# Revit family: DQ
name_source: partatom
category: Wyposażenie mechaniczne
revit_build: Autodesk Revit 2017 (Build: 20160225_1515(x64)
units: mm (PartAtom-declared; Revit-internal decimal feet)

## family parameters
Oparty na płaszczyźnie roboczej = Nie
Punkt obliczania pomieszczeń = Nie
Tnij formami wycięć po wczytaniu = Nie
Typ części = Normalny
Współdzielony = Nie
Wymiar okrągłego złącza = Użyj średnicy
Zawsze pionowo = Tak

## types (30) — shared parameters
Date = 01.2019
Frequency = 50 Hz
Producent = Rosenberg
URL = https://www.rosenberg.pl
Version = 1

## per-type parameters (varying)
- 400-4.4EC: 250_cover=Nie; 300_cover=Nie; 350_cover=Nie; 400_cover=Tak; 450_cover=Nie; 500_cover=Nie; 560_cover=Nie; 630_cover=Nie; 710_cover=Nie; 800_cover=Nie; Air_flow=3121.0 m³/h; Current=0 A; Electrical_motor_diameter=30 mm  [stored 0.0984252 ft]; Electrical_motor_length_back=60 mm  [stored 0.19685 ft]; Electrical_motor_length_front=50 mm  [stored 0.164042 ft]; Housing_dimension=540 mm; Housing_dimension/2=270 mm; Inner_diameter=403 mm; Outer_diameter=437 mm; Power=0 kW; Pressure=66.0 Pa; Propeller_length=197 mm  [stored 0.646325 ft]; Protection_class=IP54; Radius_inner=202 mm; Radius_outer=219 mm; Sheet_metal_thickness=12 mm  [stored 0.0393701 ft]; Thickness=88 mm  [stored 0.288714 ft]; Voltage=400 V; Weight=8.00 kg; max.Ambient_temperature=65 °C
- 250-2.3DF: 250_cover=Tak; 300_cover=Nie; 350_cover=Nie; 400_cover=Nie; 450_cover=Nie; 500_cover=Nie; 560_cover=Nie; 630_cover=Nie; 710_cover=Nie; 800_cover=Nie; Air_flow=0.0 m³/h; Current=0 A; Electrical_motor_diameter=30 mm  [stored 0.0984252 ft]; Electrical_motor_length_back=85 mm  [stored 0.278871 ft]; Electrical_motor_length_front=8 mm  [stored 0.0262467 ft]; Housing_dimension=370 mm; Housing_dimension/2=185 mm  [stored 0.606955 ft]; Inner_diameter=254 mm; Outer_diameter=275 mm; Power=0 kW; Pressure=0.0 Pa; Propeller_length=122 mm; Protection_class=IP44; Radius_inner=127 mm; Radius_outer=138 mm; Sheet_metal_thickness=6 mm  [stored 0.019685 ft]; Thickness=49 mm  [stored 0.160761 ft]; Voltage=400 V; Weight=4.30 kg; max.Ambient_temperature=70 °C
- 350-2: 250_cover=Nie; 300_cover=Nie; 350_cover=Tak; 400_cover=Nie; 450_cover=Nie; 500_cover=Nie; 560_cover=Nie; 630_cover=Nie; 710_cover=Nie; 800_cover=Nie; Air_flow=3693.0 m³/h; Current=2 A; Electrical_motor_diameter=30 mm  [stored 0.0984252 ft]; Electrical_motor_length_back=60 mm  [stored 0.19685 ft]; Electrical_motor_length_front=41 mm  [stored 0.134514 ft]; Housing_dimension=485 mm; Housing_dimension/2=243 mm; Inner_diameter=358 mm; Outer_diameter=381 mm; Power=1 kW; Pressure=223.0 Pa; Propeller_length=174 mm  [stored 0.570866 ft]; Protection_class=IP54; Radius_inner=179 mm  [stored 0.58727 ft]; Radius_outer=191 mm; Sheet_metal_thickness=12 mm  [stored 0.0393701 ft]; Thickness=74 mm  [stored 0.242782 ft]; Voltage=400 V; Weight=13.00 kg; max.Ambient_temperature=55 °C
- 250-4.3CF: 250_cover=Tak; 300_cover=Nie; 350_cover=Nie; 400_cover=Nie; 450_cover=Nie; 500_cover=Nie; 560_cover=Nie; 630_cover=Nie; 710_cover=Nie; 800_cover=Nie; Air_flow=0.0 m³/h; Current=0 A; Electrical_motor_diameter=30 mm  [stored 0.0984252 ft]; Electrical_motor_length_back=85 mm  [stored 0.278871 ft]; Electrical_motor_length_front=8 mm  [stored 0.0262467 ft]; Housing_dimension=370 mm; Housing_dimension/2=185 mm  [stored 0.606955 ft]; Inner_diameter=254 mm; Outer_diameter=275 mm; Power=0 kW; Pressure=0.0 Pa; Propeller_length=122 mm; Protection_class=IP44; Radius_inner=127 mm; Radius_outer=138 mm; Sheet_metal_thickness=6 mm  [stored 0.019685 ft]; Thickness=78 mm  [stored 0.255906 ft]; Voltage=230 V; Weight=4.00 kg; max.Ambient_temperature=70 °C
- 315-2: 250_cover=Nie; 300_cover=Tak; 350_cover=Nie; 400_cover=Nie; 450_cover=Nie; 500_cover=Nie; 560_cover=Nie; 630_cover=Nie; 710_cover=Nie; 800_cover=Nie; Air_flow=2675.0 m³/h; Current=1 A; Electrical_motor_diameter=30 mm  [stored 0.0984252 ft]; Electrical_motor_length_back=60 mm  [stored 0.19685 ft]; Electrical_motor_length_front=5 mm  [stored 0.0164042 ft]; Housing_dimension=430 mm; Housing_dimension/2=215 mm; Inner_diameter=317 mm; Outer_diameter=330 mm; Power=1 kW; Pressure=188.0 Pa; Propeller_length=154 mm; Protection_class=IP54; Radius_inner=159 mm; Radius_outer=165 mm; Sheet_metal_thickness=11 mm  [stored 0.0360892 ft]; Thickness=71 mm  [stored 0.23294 ft]; Voltage=400 V; Weight=9.00 kg; max.Ambient_temperature=60 °C
- 315-2.4FF: 250_cover=Nie; 300_cover=Tak; 350_cover=Nie; 400_cover=Nie; 450_cover=Nie; 500_cover=Nie; 560_cover=Nie; 630_cover=Nie; 710_cover=Nie; 800_cover=Nie; Air_flow=2310.0 m³/h; Current=1 A; Electrical_motor_diameter=30 mm  [stored 0.0984252 ft]; Electrical_motor_length_back=60 mm  [stored 0.19685 ft]; Electrical_motor_length_front=5 mm  [stored 0.0164042 ft]; Housing_dimension=430 mm; Housing_dimension/2=215 mm; Inner_diameter=317 mm; Outer_diameter=330 mm; Power=0 kW; Pressure=216.0 Pa; Propeller_length=154 mm; Protection_class=IP54; Radius_inner=159 mm; Radius_outer=165 mm; Sheet_metal_thickness=11 mm  [stored 0.0360892 ft]; Thickness=71 mm  [stored 0.23294 ft]; Voltage=40 V; Weight=5.50 kg; max.Ambient_temperature=50 °C
- 315-4.4DA: 250_cover=Nie; 300_cover=Tak; 350_cover=Nie; 400_cover=Nie; 450_cover=Nie; 500_cover=Nie; 560_cover=Nie; 630_cover=Nie; 710_cover=Nie; 800_cover=Nie; Air_flow=0.0 m³/h; Current=0 A; Electrical_motor_diameter=30 mm  [stored 0.0984252 ft]; Electrical_motor_length_back=60 mm  [stored 0.19685 ft]; Electrical_motor_length_front=5 mm  [stored 0.0164042 ft]; Housing_dimension=430 mm; Housing_dimension/2=215 mm; Inner_diameter=317 mm; Outer_diameter=330 mm; Power=0 kW; Pressure=0.0 Pa; Propeller_length=154 mm; Protection_class=IP54; Radius_inner=159 mm; Radius_outer=165 mm; Sheet_metal_thickness=11 mm  [stored 0.0360892 ft]; Thickness=71 mm  [stored 0.23294 ft]; Voltage=400 V; Weight=5.50 kg; max.Ambient_temperature=60 °C
- 350-4: 250_cover=Nie; 300_cover=Nie; 350_cover=Tak; 400_cover=Nie; 450_cover=Nie; 500_cover=Nie; 560_cover=Nie; 630_cover=Nie; 710_cover=Nie; 800_cover=Nie; Air_flow=2213.0 m³/h; Current=0 A; Electrical_motor_diameter=30 mm  [stored 0.0984252 ft]; Electrical_motor_length_back=60 mm  [stored 0.19685 ft]; Electrical_motor_length_front=41 mm  [stored 0.134514 ft]; Housing_dimension=485 mm; Housing_dimension/2=243 mm; Inner_diameter=358 mm; Outer_diameter=381 mm; Power=0 kW; Pressure=59.0 Pa; Propeller_length=174 mm  [stored 0.570866 ft]; Protection_class=IP54; Radius_inner=179 mm  [stored 0.58727 ft]; Radius_outer=191 mm; Sheet_metal_thickness=12 mm  [stored 0.0393701 ft]; Thickness=74 mm  [stored 0.242782 ft]; Voltage=400 V; Weight=6.50 kg; max.Ambient_temperature=65 °C
- 350-4.4EC: 250_cover=Nie; 300_cover=Nie; 350_cover=Tak; 400_cover=Nie; 450_cover=Nie; 500_cover=Nie; 560_cover=Nie; 630_cover=Nie; 710_cover=Nie; 800_cover=Nie; Air_flow=2079.0 m³/h; Current=0 A; Electrical_motor_diameter=30 mm  [stored 0.0984252 ft]; Electrical_motor_length_back=60 mm  [stored 0.19685 ft]; Electrical_motor_length_front=41 mm  [stored 0.134514 ft]; Housing_dimension=485 mm; Housing_dimension/2=243 mm; Inner_diameter=358 mm; Outer_diameter=381 mm; Power=0 kW; Pressure=82.0 Pa; Propeller_length=174 mm  [stored 0.570866 ft]; Protection_class=IP54; Radius_inner=179 mm  [stored 0.58727 ft]; Radius_outer=191 mm; Sheet_metal_thickness=12 mm  [stored 0.0393701 ft]; Thickness=74 mm  [stored 0.242782 ft]; Voltage=400 V; Weight=7.00 kg; max.Ambient_temperature=70 °C
- 400-6: 250_cover=Nie; 300_cover=Nie; 350_cover=Nie; 400_cover=Tak; 450_cover=Nie; 500_cover=Nie; 560_cover=Nie; 630_cover=Nie; 710_cover=Nie; 800_cover=Nie; Air_flow=2565.0 m³/h; Current=0 A; Electrical_motor_diameter=65 mm  [stored 0.213255 ft]; Electrical_motor_length_back=60 mm  [stored 0.19685 ft]; Electrical_motor_length_front=50 mm  [stored 0.164042 ft]; Housing_dimension=540 mm; Housing_dimension/2=270 mm; Inner_diameter=403 mm; Outer_diameter=437 mm; Power=0 kW; Pressure=46.0 Pa; Propeller_length=197 mm  [stored 0.646325 ft]; Protection_class=IP54; Radius_inner=202 mm; Radius_outer=219 mm; Sheet_metal_thickness=12 mm  [stored 0.0393701 ft]; Thickness=88 mm  [stored 0.288714 ft]; Voltage=400 V; Weight=9.00 kg; max.Ambient_temperature=60 °C
- 450-4.5DF: 250_cover=Nie; 300_cover=Nie; 350_cover=Nie; 400_cover=Nie; 450_cover=Tak; 500_cover=Nie; 560_cover=Nie; 630_cover=Nie; 710_cover=Nie; 800_cover=Nie; Air_flow=4246.0 m³/h; Current=1 A; Electrical_motor_diameter=65 mm  [stored 0.213255 ft]; Electrical_motor_length_back=60 mm  [stored 0.19685 ft]; Electrical_motor_length_front=50 mm  [stored 0.164042 ft]; Housing_dimension=575 mm; Housing_dimension/2=288 mm; Inner_diameter=452 mm; Outer_diameter=513 mm; Power=0 kW; Pressure=96.0 Pa; Propeller_length=221 mm; Protection_class=IP54; Radius_inner=226 mm; Radius_outer=257 mm; Sheet_metal_thickness=14 mm  [stored 0.0459318 ft]; Thickness=86 mm  [stored 0.282152 ft]; Voltage=400 V; Weight=10.50 kg; max.Ambient_temperature=60 °C
- 450-6.5DF: 250_cover=Nie; 300_cover=Nie; 350_cover=Nie; 400_cover=Nie; 450_cover=Tak; 500_cover=Nie; 560_cover=Nie; 630_cover=Nie; 710_cover=Nie; 800_cover=Nie; Air_flow=0.0 m³/h; Current=0 A; Electrical_motor_diameter=65 mm  [stored 0.213255 ft]; Electrical_motor_length_back=60 mm  [stored 0.19685 ft]; Electrical_motor_length_front=50 mm  [stored 0.164042 ft]; Housing_dimension=575 mm; Housing_dimension/2=288 mm; Inner_diameter=452 mm; Outer_diameter=513 mm; Power=0 kW; Pressure=0.0 Pa; Propeller_length=221 mm; Protection_class=IP54; Radius_inner=226 mm; Radius_outer=257 mm; Sheet_metal_thickness=14 mm  [stored 0.0459318 ft]; Thickness=86 mm  [stored 0.282152 ft]; Voltage=400 V; Weight=10.00 kg; max.Ambient_temperature=70 °C
- 500-4.5FA: 250_cover=Nie; 300_cover=Nie; 350_cover=Nie; 400_cover=Nie; 450_cover=Nie; 500_cover=Tak; 560_cover=Nie; 630_cover=Nie; 710_cover=Nie; 800_cover=Nie; Air_flow=5256.0 m³/h; Current=1 A; Electrical_motor_diameter=65 mm  [stored 0.213255 ft]; Electrical_motor_length_back=60 mm  [stored 0.19685 ft]; Electrical_motor_length_front=50 mm  [stored 0.164042 ft]; Housing_dimension=655 mm; Housing_dimension/2=328 mm; Inner_diameter=504 mm; Outer_diameter=540 mm; Power=0 kW; Pressure=105.0 Pa; Propeller_length=247 mm; Protection_class=IP54; Radius_inner=252 mm; Radius_outer=270 mm; Sheet_metal_thickness=16 mm  [stored 0.0524934 ft]; Thickness=104 mm  [stored 0.341207 ft]; Voltage=400 V; Weight=15.50 kg; max.Ambient_temperature=60 °C
- 560-4.5HA: 250_cover=Nie; 300_cover=Nie; 350_cover=Nie; 400_cover=Nie; 450_cover=Nie; 500_cover=Nie; 560_cover=Tak; 630_cover=Nie; 710_cover=Nie; 800_cover=Nie; Air_flow=6766.0 m³/h; Current=2 A; Electrical_motor_diameter=65 mm  [stored 0.213255 ft]; Electrical_motor_length_back=60 mm  [stored 0.19685 ft]; Electrical_motor_length_front=50 mm  [stored 0.164042 ft]; Housing_dimension=725 mm; Housing_dimension/2=363 mm; Inner_diameter=560 mm; Outer_diameter=597 mm; Power=1 kW; Pressure=136.0 Pa; Propeller_length=275 mm; Protection_class=IP54; Radius_inner=280 mm; Radius_outer=299 mm; Sheet_metal_thickness=16 mm  [stored 0.0524934 ft]; Thickness=104 mm  [stored 0.341207 ft]; Voltage=400 V; Weight=19.50 kg; max.Ambient_temperature=50 °C
- 560-6.5FA: 250_cover=Nie; 300_cover=Nie; 350_cover=Nie; 400_cover=Nie; 450_cover=Nie; 500_cover=Nie; 560_cover=Tak; 630_cover=Nie; 710_cover=Nie; 800_cover=Nie; Air_flow=5438.0 m³/h; Current=1 A; Electrical_motor_diameter=65 mm  [stored 0.213255 ft]; Electrical_motor_length_back=60 mm  [stored 0.19685 ft]; Electrical_motor_length_front=50 mm  [stored 0.164042 ft]; Housing_dimension=725 mm; Housing_dimension/2=363 mm; Inner_diameter=560 mm; Outer_diameter=597 mm; Power=0 kW; Pressure=69.0 Pa; Propeller_length=275 mm; Protection_class=IP54; Radius_inner=280 mm; Radius_outer=299 mm; Sheet_metal_thickness=16 mm  [stored 0.0524934 ft]; Thickness=104 mm  [stored 0.341207 ft]; Voltage=400 V; Weight=20.00 kg; max.Ambient_temperature=55 °C
- 630-4: 250_cover=Nie; 300_cover=Nie; 350_cover=Nie; 400_cover=Nie; 450_cover=Nie; 500_cover=Nie; 560_cover=Nie; 630_cover=Tak; 710_cover=Nie; 800_cover=Nie; Air_flow=12190.0 m³/h; Current=4 A; Electrical_motor_diameter=65 mm  [stored 0.213255 ft]; Electrical_motor_length_back=60 mm  [stored 0.19685 ft]; Electrical_motor_length_front=50 mm  [stored 0.164042 ft]; Housing_dimension=805 mm; Housing_dimension/2=403 mm; Inner_diameter=635 mm; Outer_diameter=683 mm; Power=2 kW; Pressure=209.0 Pa; Propeller_length=313 mm; Protection_class=IP44; Radius_inner=318 mm; Radius_outer=342 mm; Sheet_metal_thickness=20 mm  [stored 0.0656168 ft]; Thickness=130 mm  [stored 0.426509 ft]; Voltage=400 V; Weight=35.00 kg; max.Ambient_temperature=50 °C
- 630-6.5HA: 250_cover=Nie; 300_cover=Nie; 350_cover=Nie; 400_cover=Nie; 450_cover=Nie; 500_cover=Nie; 560_cover=Nie; 630_cover=Tak; 710_cover=Nie; 800_cover=Nie; Air_flow=7885.0 m³/h; Current=1 A; Electrical_motor_diameter=65 mm  [stored 0.213255 ft]; Electrical_motor_length_back=60 mm  [stored 0.19685 ft]; Electrical_motor_length_front=50 mm  [stored 0.164042 ft]; Housing_dimension=805 mm; Housing_dimension/2=403 mm; Inner_diameter=635 mm; Outer_diameter=683 mm; Power=1 kW; Pressure=74.0 Pa; Propeller_length=313 mm; Protection_class=IP54; Radius_inner=318 mm; Radius_outer=342 mm; Sheet_metal_thickness=20 mm  [stored 0.0656168 ft]; Thickness=130 mm  [stored 0.426509 ft]; Voltage=400 V; Weight=22.00 kg; max.Ambient_temperature=55 °C
- 710-6.6HF: 250_cover=Nie; 300_cover=Nie; 350_cover=Nie; 400_cover=Nie; 450_cover=Nie; 500_cover=Nie; 560_cover=Nie; 630_cover=Nie; 710_cover=Tak; 800_cover=Nie; Air_flow=10492.0 m³/h; Current=2 A; Electrical_motor_diameter=50 mm  [stored 0.164042 ft]; Electrical_motor_length_back=60 mm  [stored 0.19685 ft]; Electrical_motor_length_front=50 mm  [stored 0.164042 ft]; Housing_dimension=850 mm; Housing_dimension/2=425 mm; Inner_diameter=711 mm; Outer_diameter=772 mm; Power=1 kW; Pressure=104.0 Pa; Propeller_length=351 mm; Protection_class=IP54; Radius_inner=356 mm; Radius_outer=386 mm; Sheet_metal_thickness=20 mm  [stored 0.0656168 ft]; Thickness=150 mm; Voltage=400 V; Weight=36.00 kg; max.Ambient_temperature=70 °C
- 500-6.5DF: 250_cover=Nie; 300_cover=Nie; 350_cover=Nie; 400_cover=Nie; 450_cover=Nie; 500_cover=Tak; 560_cover=Nie; 630_cover=Nie; 710_cover=Nie; 800_cover=Nie; Air_flow=3433.0 m³/h; Current=0 A; Electrical_motor_diameter=65 mm  [stored 0.213255 ft]; Electrical_motor_length_back=60 mm  [stored 0.19685 ft]; Electrical_motor_length_front=50 mm  [stored 0.164042 ft]; Housing_dimension=655 mm; Housing_dimension/2=328 mm; Inner_diameter=504 mm; Outer_diameter=540 mm; Power=0 kW; Pressure=49.0 Pa; Propeller_length=247 mm; Protection_class=IP54; Radius_inner=252 mm; Radius_outer=270 mm; Sheet_metal_thickness=16 mm  [stored 0.0524934 ft]; Thickness=104 mm  [stored 0.341207 ft]; Voltage=400 V; Weight=16.00 kg; max.Ambient_temperature=70 °C
- 630-4.6LA: 250_cover=Nie; 300_cover=Nie; 350_cover=Nie; 400_cover=Nie; 450_cover=Nie; 500_cover=Nie; 560_cover=Nie; 630_cover=Tak; 710_cover=Nie; 800_cover=Nie; Air_flow=12440.0 m³/h; Current=4 A; Electrical_motor_diameter=65 mm  [stored 0.213255 ft]; Electrical_motor_length_back=60 mm  [stored 0.19685 ft]; Electrical_motor_length_front=50 mm  [stored 0.164042 ft]; Housing_dimension=805 mm; Housing_dimension/2=403 mm; Inner_diameter=635 mm; Outer_diameter=683 mm; Power=2 kW; Pressure=243.0 Pa; Propeller_length=313 mm; Protection_class=IP54; Radius_inner=318 mm; Radius_outer=342 mm; Sheet_metal_thickness=20 mm  [stored 0.0656168 ft]; Thickness=130 mm  [stored 0.426509 ft]; Voltage=400 V; Weight=39.00 kg; max.Ambient_temperature=65 °C
- 800-6.6HF: 250_cover=Nie; 300_cover=Nie; 350_cover=Nie; 400_cover=Nie; 450_cover=Nie; 500_cover=Nie; 560_cover=Nie; 630_cover=Nie; 710_cover=Nie; 800_cover=Tak; Air_flow=13705.0 m³/h; Current=3 A; Electrical_motor_diameter=50 mm  [stored 0.164042 ft]; Electrical_motor_length_back=60 mm  [stored 0.19685 ft]; Electrical_motor_length_front=50 mm  [stored 0.164042 ft]; Housing_dimension=970 mm; Housing_dimension/2=485 mm; Inner_diameter=798 mm; Outer_diameter=857 mm; Power=1 kW; Pressure=121.0 Pa; Propeller_length=394 mm; Protection_class=IP54; Radius_inner=399 mm; Radius_outer=429 mm; Sheet_metal_thickness=20 mm  [stored 0.0656168 ft]; Thickness=190 mm  [stored 0.62336 ft]; Voltage=400 V; Weight=41.00 kg; max.Ambient_temperature=70 °C
- 1000-12.7KF: 250_cover=Nie; 300_cover=Nie; 350_cover=Nie; 400_cover=Nie; 450_cover=Nie; 500_cover=Nie; 560_cover=Nie; 630_cover=Nie; 710_cover=Nie; 800_cover=Nie; Air_flow=15215.0 m³/h; Current=2 A; Electrical_motor_diameter=50 mm  [stored 0.164042 ft]; Electrical_motor_length_back=60 mm  [stored 0.19685 ft]; Electrical_motor_length_front=50 mm  [stored 0.164042 ft]; Housing_dimension=1110 mm; Housing_dimension/2=555 mm; Inner_diameter=1000 mm; Outer_diameter=1064 mm; Power=1 kW; Pressure=55.0 Pa; Propeller_length=495 mm; Protection_class=IP54; Radius_inner=500 mm; Radius_outer=532 mm; Sheet_metal_thickness=20 mm  [stored 0.0656168 ft]; Thickness=217 mm; Voltage=400 V; Weight=65.00 kg; max.Ambient_temperature=80 °C
- 1000-8.7NA: 250_cover=Nie; 300_cover=Nie; 350_cover=Nie; 400_cover=Nie; 450_cover=Nie; 500_cover=Nie; 560_cover=Nie; 630_cover=Nie; 710_cover=Nie; 800_cover=Nie; Air_flow=24893.0 m³/h; Current=4 A; Electrical_motor_diameter=50 mm  [stored 0.164042 ft]; Electrical_motor_length_back=60 mm  [stored 0.19685 ft]; Electrical_motor_length_front=50 mm  [stored 0.164042 ft]; Housing_dimension=1110 mm; Housing_dimension/2=555 mm; Inner_diameter=1000 mm; Outer_diameter=1064 mm; Power=2 kW; Pressure=105.0 Pa; Propeller_length=495 mm; Protection_class=IP54; Radius_inner=500 mm; Radius_outer=532 mm; Sheet_metal_thickness=20 mm  [stored 0.0656168 ft]; Thickness=217 mm; Voltage=400 V; Weight=71.00 kg; max.Ambient_temperature=55 °C
- 315-4 Zone 2: 250_cover=Nie; 300_cover=Tak; 350_cover=Nie; 400_cover=Nie; 450_cover=Nie; 500_cover=Nie; 560_cover=Nie; 630_cover=Nie; 710_cover=Nie; 800_cover=Nie; Air_flow=0.0 m³/h; Current=0 A; Electrical_motor_diameter=30 mm  [stored 0.0984252 ft]; Electrical_motor_length_back=60 mm  [stored 0.19685 ft]; Electrical_motor_length_front=5 mm  [stored 0.0164042 ft]; Housing_dimension=430 mm; Housing_dimension/2=215 mm; Inner_diameter=317 mm; Outer_diameter=335 mm; Power=0 kW; Pressure=0.0 Pa; Propeller_length=154 mm; Protection_class=IP54; Radius_inner=159 mm; Radius_outer=168 mm  [stored 0.551181 ft]; Sheet_metal_thickness=11 mm  [stored 0.0360892 ft]; Thickness=71 mm  [stored 0.23294 ft]; Voltage=400 V; Weight=0.00 kg; max.Ambient_temperature=40 °C
- 350-4 Zone 2: 250_cover=Nie; 300_cover=Nie; 350_cover=Tak; 400_cover=Nie; 450_cover=Nie; 500_cover=Nie; 560_cover=Nie; 630_cover=Nie; 710_cover=Nie; 800_cover=Nie; Air_flow=0.0 m³/h; Current=0 A; Electrical_motor_diameter=30 mm  [stored 0.0984252 ft]; Electrical_motor_length_back=60 mm  [stored 0.19685 ft]; Electrical_motor_length_front=41 mm  [stored 0.134514 ft]; Housing_dimension=485 mm; Housing_dimension/2=243 mm; Inner_diameter=358 mm; Outer_diameter=385 mm; Power=0 kW; Pressure=0.0 Pa; Propeller_length=174 mm  [stored 0.570866 ft]; Protection_class=IP54; Radius_inner=179 mm  [stored 0.58727 ft]; Radius_outer=193 mm; Sheet_metal_thickness=12 mm  [stored 0.0393701 ft]; Thickness=74 mm  [stored 0.242782 ft]; Voltage=400 V; Weight=0.00 kg; max.Ambient_temperature=40 °C
- 400-4 Zone 2: 250_cover=Nie; 300_cover=Nie; 350_cover=Nie; 400_cover=Tak; 450_cover=Nie; 500_cover=Nie; 560_cover=Nie; 630_cover=Nie; 710_cover=Nie; 800_cover=Nie; Air_flow=0.0 m³/h; Current=0 A; Electrical_motor_diameter=30 mm  [stored 0.0984252 ft]; Electrical_motor_length_back=60 mm  [stored 0.19685 ft]; Electrical_motor_length_front=50 mm  [stored 0.164042 ft]; Housing_dimension=540 mm; Housing_dimension/2=270 mm; Inner_diameter=403 mm; Outer_diameter=445 mm; Power=0 kW; Pressure=0.0 Pa; Propeller_length=197 mm  [stored 0.646325 ft]; Protection_class=IP44; Radius_inner=202 mm; Radius_outer=223 mm; Sheet_metal_thickness=12 mm  [stored 0.0393701 ft]; Thickness=88 mm  [stored 0.288714 ft]; Voltage=400 V; Weight=0.00 kg; max.Ambient_temperature=40 °C
- 450-4 Zone 2: 250_cover=Nie; 300_cover=Nie; 350_cover=Nie; 400_cover=Nie; 450_cover=Tak; 500_cover=Nie; 560_cover=Nie; 630_cover=Nie; 710_cover=Nie; 800_cover=Nie; Air_flow=0.0 m³/h; Current=1 A; Electrical_motor_diameter=65 mm  [stored 0.213255 ft]; Electrical_motor_length_back=60 mm  [stored 0.19685 ft]; Electrical_motor_length_front=50 mm  [stored 0.164042 ft]; Housing_dimension=575 mm; Housing_dimension/2=288 mm; Inner_diameter=452 mm; Outer_diameter=495 mm; Power=0 kW; Pressure=0.0 Pa; Propeller_length=221 mm; Protection_class=IP44; Radius_inner=226 mm; Radius_outer=248 mm; Sheet_metal_thickness=14 mm  [stored 0.0459318 ft]; Thickness=86 mm  [stored 0.282152 ft]; Voltage=400 V; Weight=0.00 kg; max.Ambient_temperature=40 °C
- 500-4 Zone 2: 250_cover=Nie; 300_cover=Nie; 350_cover=Nie; 400_cover=Nie; 450_cover=Nie; 500_cover=Tak; 560_cover=Nie; 630_cover=Nie; 710_cover=Nie; 800_cover=Nie; Air_flow=0.0 m³/h; Current=1 A; Electrical_motor_diameter=65 mm  [stored 0.213255 ft]; Electrical_motor_length_back=60 mm  [stored 0.19685 ft]; Electrical_motor_length_front=50 mm  [stored 0.164042 ft]; Housing_dimension=655 mm; Housing_dimension/2=328 mm; Inner_diameter=504 mm; Outer_diameter=540 mm; Power=0 kW; Pressure=0.0 Pa; Propeller_length=247 mm; Protection_class=IP44; Radius_inner=252 mm; Radius_outer=270 mm; Sheet_metal_thickness=16 mm  [stored 0.0524934 ft]; Thickness=104 mm  [stored 0.341207 ft]; Voltage=400 V; Weight=0.00 kg; max.Ambient_temperature=40 °C
- 560-6 Zone 2: 250_cover=Nie; 300_cover=Nie; 350_cover=Nie; 400_cover=Nie; 450_cover=Nie; 500_cover=Nie; 560_cover=Tak; 630_cover=Nie; 710_cover=Nie; 800_cover=Nie; Air_flow=0.0 m³/h; Current=1 A; Electrical_motor_diameter=65 mm  [stored 0.213255 ft]; Electrical_motor_length_back=60 mm  [stored 0.19685 ft]; Electrical_motor_length_front=50 mm  [stored 0.164042 ft]; Housing_dimension=725 mm; Housing_dimension/2=363 mm; Inner_diameter=560 mm; Outer_diameter=605 mm; Power=0 kW; Pressure=0.0 Pa; Propeller_length=275 mm; Protection_class=IP44; Radius_inner=280 mm; Radius_outer=303 mm; Sheet_metal_thickness=16 mm  [stored 0.0524934 ft]; Thickness=104 mm  [stored 0.341207 ft]; Voltage=400 V; Weight=0.00 kg; max.Ambient_temperature=40 °C
- 630-6 Zone 2: 250_cover=Nie; 300_cover=Nie; 350_cover=Nie; 400_cover=Nie; 450_cover=Nie; 500_cover=Nie; 560_cover=Nie; 630_cover=Tak; 710_cover=Nie; 800_cover=Nie; Air_flow=0.0 m³/h; Current=1 A; Electrical_motor_diameter=65 mm  [stored 0.213255 ft]; Electrical_motor_length_back=60 mm  [stored 0.19685 ft]; Electrical_motor_length_front=50 mm  [stored 0.164042 ft]; Housing_dimension=805 mm; Housing_dimension/2=403 mm; Inner_diameter=635 mm; Outer_diameter=690 mm; Power=1 kW; Pressure=0.0 Pa; Propeller_length=313 mm; Protection_class=IP44; Radius_inner=318 mm; Radius_outer=345 mm; Sheet_metal_thickness=20 mm  [stored 0.0656168 ft]; Thickness=130 mm  [stored 0.426509 ft]; Voltage=400 V; Weight=0.00 kg; max.Ambient_temperature=40 °C

note: column(s) folded — value = type name in every type: Model

note: [stored X ft] marks values corroborated as IEEE doubles in the binary element streams (Revit-internal decimal feet)
